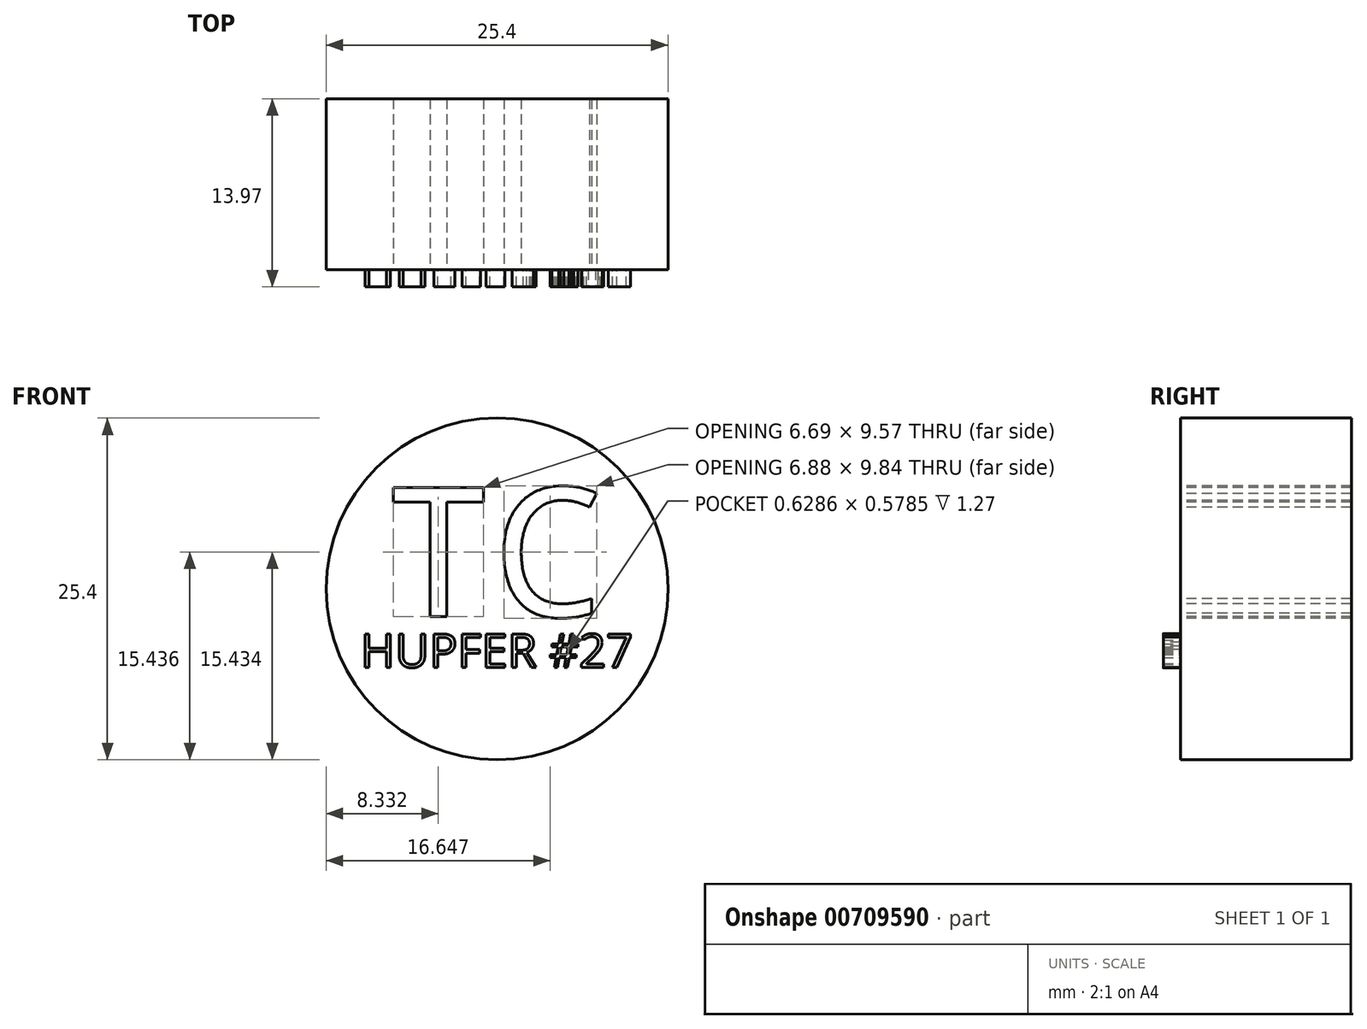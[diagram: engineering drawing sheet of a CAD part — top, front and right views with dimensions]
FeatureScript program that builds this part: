
annotation { "Feature Type Name" : "Feature", "Feature Type Description" : "" }
export const myFeature = defineFeature(function(context is Context, id is Id, definition is map)
    precondition{}
    {
        {
            var Q0;
            Q0=qCreatedBy(makeId("Front.planeOp"),FACE);
            var sketch = newSketch(context, id + "F0", { "sketchPlane" : qUnion([Q0])});
            skCircle(sketch, "E0", {"center": v(-44.07, 49.18) * mm, "radius": 12.7 * mm});
            skSolve(sketch);
        }
        {
            var Q0;
            Q0=qSketchRegion(id+"F0",true);
            extrude(context, id + "F1", {"entities" : qUnion([Q0]), "depth" : 12.7 * mm, "offsetDistance" : 25.4 * mm});
        }
        {
            var Q0;
            Q0=makeQuery(id+"F1.opExtrude","CAP_FACE",FACE,{"disambiguationData":[OSD([sQuery(id+"F0.wireOp",EDGE,"E0")])],"isStart":false});
            var sketch = newSketch(context, id + "F2", { "sketchPlane" : qUnion([Q0])});
            skText(sketch, "E1", { "text": "TC", "fontName": "DroidSansMono.ttf"});
            const initialGuessF2  = {"E1": [-0.05245, 0.04713, 1, 0, 0.00965]};
            skSetInitialGuess(sketch, initialGuessF2);
            skSolve(sketch);
        }
        {
            var Q0;
            Q0=qSketchRegion(id+"F2",true);
            extrude(context, id + "F3", {"entities" : qUnion([Q0]), "operationType" : NewBodyOperationType.ADD, "depth" : 1.27 * mm, "offsetDistance" : 25.4 * mm});
        }
        {
            var Q0;
            Q0=makeQuery(id+"F1.opExtrude","CAP_FACE",FACE,{"disambiguationData":[OSD([sQuery(id+"F0.wireOp",EDGE,"E0")])],"isStart":false});
            var sketch = newSketch(context, id + "F4", { "sketchPlane" : qUnion([Q0])});
            skText(sketch, "E2", { "text": "HUPFER #27", "fontName": "OpenSans-Regular.ttf"});
            const initialGuessF4  = {"E2": [-0.05423, 0.04334, 1, 0, 0.00251]};
            skSetInitialGuess(sketch, initialGuessF4);
            skSolve(sketch);
        }
        {
            var Q0;
            Q0=qSketchRegion(id+"F4",true);
            extrude(context, id + "F5", {"entities" : qUnion([Q0]), "operationType" : NewBodyOperationType.ADD, "depth" : 1.27 * mm, "offsetDistance" : 25.4 * mm});
        }
        {
            var Q0;
            Q0=makeQuery(id+"F3.opExtrude","CAP_FACE",FACE,{"disambiguationData":[OSD([sQuery(id+"F2.wireOp",EDGE,"E1.sketch_text.stroke-0"),sQuery(id+"F2.wireOp",EDGE,"E1.sketch_text.stroke-1"),sQuery(id+"F2.wireOp",EDGE,"E1.sketch_text.stroke-2"),sQuery(id+"F2.wireOp",EDGE,"E1.sketch_text.stroke-3"),sQuery(id+"F2.wireOp",EDGE,"E1.sketch_text.stroke-4"),sQuery(id+"F2.wireOp",EDGE,"E1.sketch_text.stroke-5"),sQuery(id+"F2.wireOp",EDGE,"E1.sketch_text.stroke-6"),sQuery(id+"F2.wireOp",EDGE,"E1.sketch_text.stroke-7")])],"isStart":false});
            extrude(context, id + "F6", {"entities" : qUnion([Q0]), "operationType" : NewBodyOperationType.REMOVE, "endBound" : BoundingType.THROUGH_ALL, "oppositeDirection" : true, "depth" : 25.4 * mm, "offsetDistance" : 25.4 * mm});
        }
        {
            var Q0;
            Q0=makeQuery(id+"F3.opExtrude","CAP_FACE",FACE,{"disambiguationData":[OSD([sQuery(id+"F2.wireOp",EDGE,"E1.sketch_text.stroke-8"),sQuery(id+"F2.wireOp",EDGE,"E1.sketch_text.stroke-9"),sQuery(id+"F2.wireOp",EDGE,"E1.sketch_text.stroke-10"),sQuery(id+"F2.wireOp",EDGE,"E1.sketch_text.stroke-11"),sQuery(id+"F2.wireOp",EDGE,"E1.sketch_text.stroke-12"),sQuery(id+"F2.wireOp",EDGE,"E1.sketch_text.stroke-13"),sQuery(id+"F2.wireOp",EDGE,"E1.sketch_text.stroke-14"),sQuery(id+"F2.wireOp",EDGE,"E1.sketch_text.stroke-15"),sQuery(id+"F2.wireOp",EDGE,"E1.sketch_text.stroke-16"),sQuery(id+"F2.wireOp",EDGE,"E1.sketch_text.stroke-17"),sQuery(id+"F2.wireOp",EDGE,"E1.sketch_text.stroke-18"),sQuery(id+"F2.wireOp",EDGE,"E1.sketch_text.stroke-19"),sQuery(id+"F2.wireOp",EDGE,"E1.sketch_text.stroke-20"),sQuery(id+"F2.wireOp",EDGE,"E1.sketch_text.stroke-21")])],"isStart":false});
            extrude(context, id + "F7", {"entities" : qUnion([Q0]), "operationType" : NewBodyOperationType.REMOVE, "endBound" : BoundingType.THROUGH_ALL, "oppositeDirection" : true, "depth" : 25.4 * mm, "offsetDistance" : 25.4 * mm});
        }
    });
